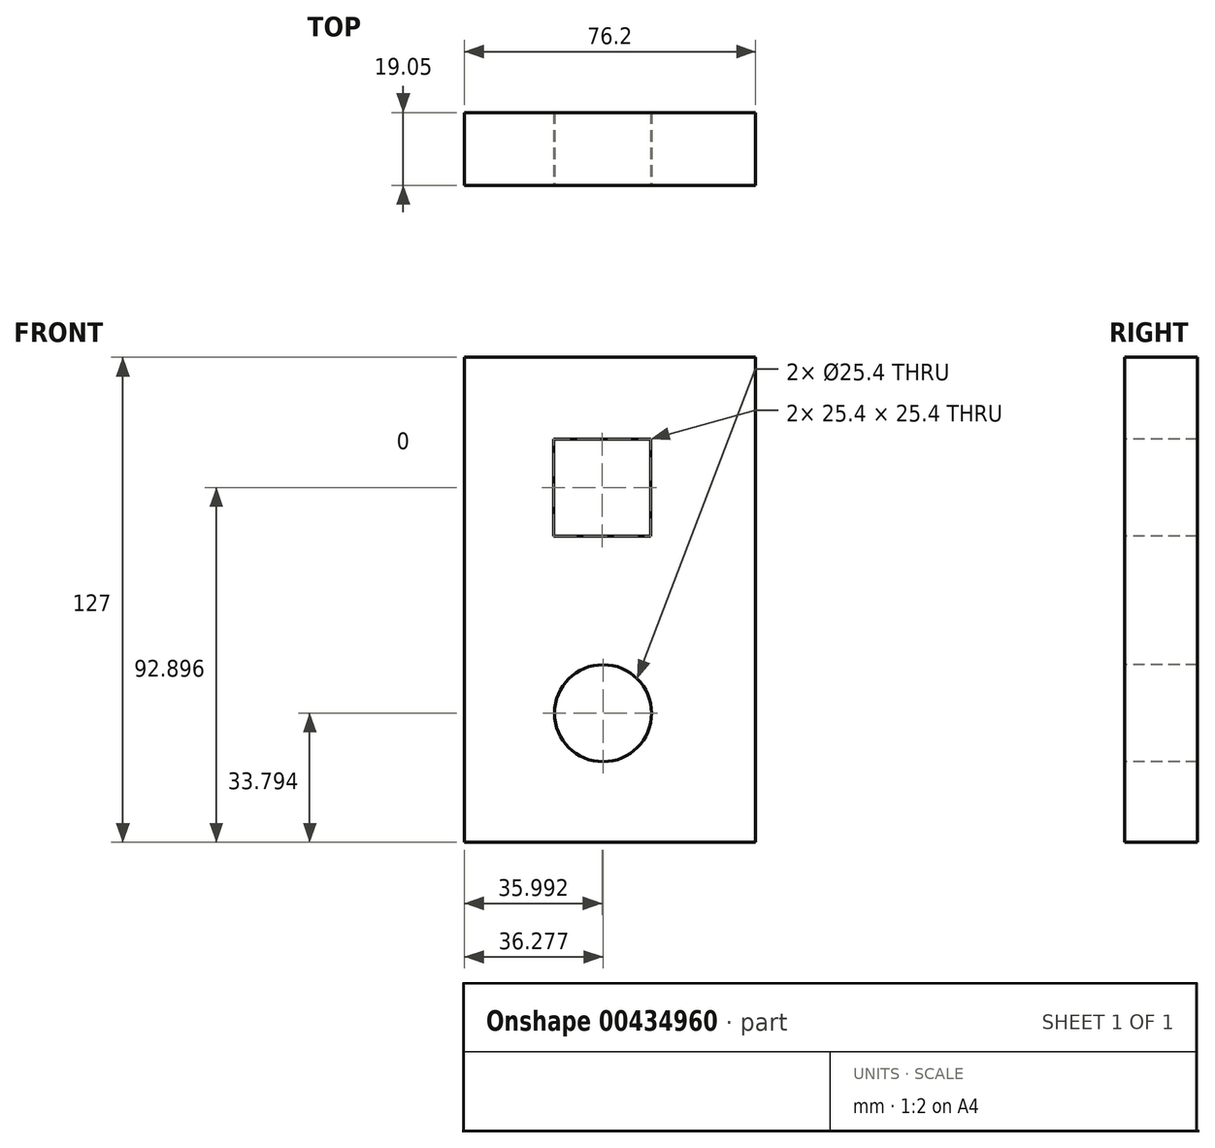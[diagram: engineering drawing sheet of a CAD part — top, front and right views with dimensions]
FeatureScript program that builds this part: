
annotation { "Feature Type Name" : "Feature", "Feature Type Description" : "" }
export const myFeature = defineFeature(function(context is Context, id is Id, definition is map)
    precondition{}
    {
        {
            var Q0;
            Q0=qCreatedBy(makeId("Front.planeOp"),FACE);
            var sketch = newSketch(context, id + "F0", { "sketchPlane" : qUnion([Q0])});
            skLineSegment(sketch, "E0.bottom", {"start": v(-58.81, 54.06) * mm, "end": v(17.39, 54.06) * mm});
            skLineSegment(sketch, "E0.top", {"start": v(-58.81, -72.94) * mm, "end": v(17.39, -72.94) * mm});
            skLineSegment(sketch, "E0.left", {"start": v(-58.81, 54.06) * mm, "end": v(-58.81, -72.94) * mm});
            skLineSegment(sketch, "E0.right", {"start": v(17.39, 54.06) * mm, "end": v(17.39, -72.94) * mm});
            skSolve(sketch);
        }
        {
            var Q0;
            Q0=makeQuery(id+"F0.imprint","IMPRINT",FACE,{"disambiguationData":[TD([[makeQuery(id+"F0.imprint","IMPRINT",EDGE,{"derivedFrom":sQuery(id+"F0.wireOp",EDGE,"E0.bottom")}),-1.0]])]});
            extrude(context, id + "F1", {"entities" : qUnion([Q0]), "depth" : 19.05 * mm});
        }
        {
            var Q0;
            Q0=makeQuery(id+"F1.opExtrude","CAP_FACE",FACE,{"disambiguationData":[OSD([sQuery(id+"F0.wireOp",EDGE,"E0.bottom"),sQuery(id+"F0.wireOp",EDGE,"E0.top"),sQuery(id+"F0.wireOp",EDGE,"E0.left"),sQuery(id+"F0.wireOp",EDGE,"E0.right")])],"isStart":false});
            var sketch = newSketch(context, id + "F2", { "sketchPlane" : qUnion([Q0])});
            skCircle(sketch, "E1", {"center": v(-22.53, -39.15) * mm, "radius": 12.7 * mm});
            skLineSegment(sketch, "E2.bottom", {"start": v(-9.35, 9.93) * mm, "end": v(-34.75, 9.93) * mm});
            skLineSegment(sketch, "E2.top", {"start": v(-9.35, 35.33) * mm, "end": v(-34.75, 35.33) * mm});
            skLineSegment(sketch, "E2.left", {"start": v(-9.35, 9.93) * mm, "end": v(-9.35, 35.33) * mm});
            skLineSegment(sketch, "E2.right", {"start": v(-34.75, 9.93) * mm, "end": v(-34.75, 35.33) * mm});
            skSolve(sketch);
        }
        {
            var Q0;
            Q0=makeQuery(id+"F2.imprint","IMPRINT",FACE,{"disambiguationData":[TD([[makeQuery(id+"F2.imprint","IMPRINT",EDGE,{"derivedFrom":sQuery(id+"F2.wireOp",EDGE,"E1")}),1.0]])]});
            extrude(context, id + "F3", {"entities" : qUnion([Q0]), "operationType" : NewBodyOperationType.REMOVE, "oppositeDirection" : true, "depth" : 25.4 * mm});
        }
        {
            var Q0;
            Q0=makeQuery(id+"F1.opExtrude","CAP_FACE",FACE,{"disambiguationData":[OSD([sQuery(id+"F0.wireOp",EDGE,"E0.bottom"),sQuery(id+"F0.wireOp",EDGE,"E0.top"),sQuery(id+"F0.wireOp",EDGE,"E0.left"),sQuery(id+"F0.wireOp",EDGE,"E0.right")])],"isStart":false});
            var sketch = newSketch(context, id + "F4", { "sketchPlane" : qUnion([Q0])});
            skLineSegment(sketch, "E3.bottom", {"start": v(-10.12, 7.26) * mm, "end": v(-35.52, 7.26) * mm});
            skLineSegment(sketch, "E3.top", {"start": v(-10.12, 32.66) * mm, "end": v(-35.52, 32.66) * mm});
            skLineSegment(sketch, "E3.left", {"start": v(-10.12, 7.26) * mm, "end": v(-10.12, 32.66) * mm});
            skLineSegment(sketch, "E3.right", {"start": v(-35.52, 7.26) * mm, "end": v(-35.52, 32.66) * mm});
            skSolve(sketch);
        }
        {
            var Q0;
            Q0=makeQuery(id+"F4.imprint","IMPRINT",FACE,{"disambiguationData":[TD([[makeQuery(id+"F4.imprint","IMPRINT",EDGE,{"derivedFrom":sQuery(id+"F4.wireOp",EDGE,"E3.bottom")}),-1.0]])]});
            extrude(context, id + "F5", {"entities" : qUnion([Q0]), "operationType" : NewBodyOperationType.REMOVE, "oppositeDirection" : true, "depth" : 25.4 * mm});
        }
    });
